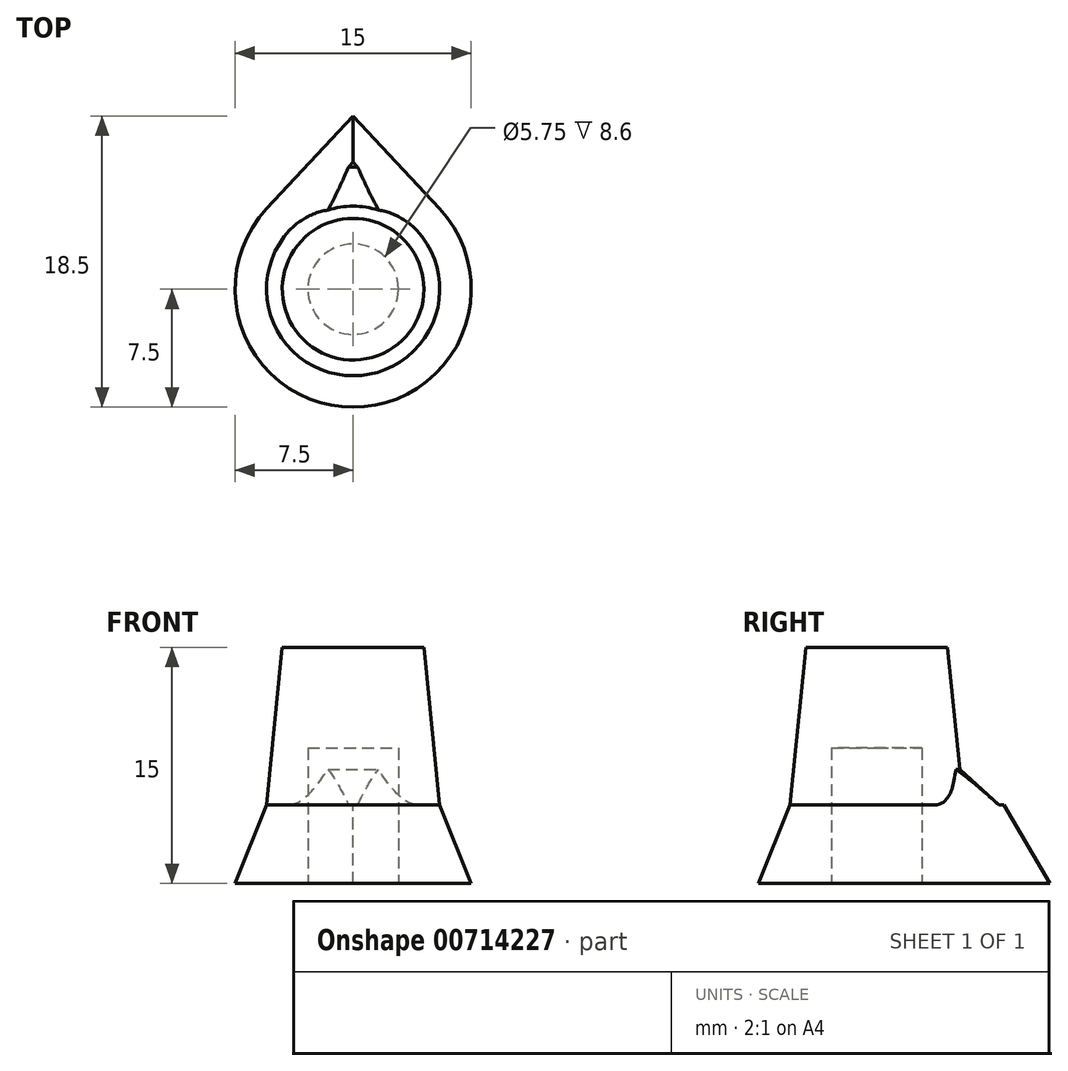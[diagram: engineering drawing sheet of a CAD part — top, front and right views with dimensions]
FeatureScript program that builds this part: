
annotation { "Feature Type Name" : "Feature", "Feature Type Description" : "" }
export const myFeature = defineFeature(function(context is Context, id is Id, definition is map)
    precondition{}
    {
        {
            var Q0;
            Q0=qCreatedBy(makeId("Top.planeOp"),FACE);
            var sketch = newSketch(context, id + "F0", { "sketchPlane" : qUnion([Q0])});
            skArc(sketch, "E0", {"start": v(-5.49, 5.11) * mm, "mid": v(0, -7.5) * mm, "end": v(5.49, 5.11) * mm});
            skLineSegment(sketch, "E1", {"start": v(-5.49, 5.11) * mm, "end": v(0, 11) * mm});
            skLineSegment(sketch, "E2", {"start": v(0, 11) * mm, "end": v(0, 0) * mm, "construction": true});
            skLineSegment(sketch, "E3.MirrorCS", {"start": v(5.49, 5.11) * mm, "end": v(0, 11) * mm});
            skSolve(sketch);
        }
        {
            var Q0;
            Q0=qCreatedBy(makeId("Top.planeOp"),FACE);
            cPlane(context, id + "F1", {"entities" : qUnion([Q0]), "cplaneType" : CPlaneType.OFFSET, "offset" : 5 * mm, "width" : 150 * mm, "height" : 150 * mm});
        }
        {
            var Q0;
            Q0=qCreatedBy(id+"F1.planeOp",FACE);
            var sketch = newSketch(context, id + "F2", { "sketchPlane" : qUnion([Q0])});
            skLineSegment(sketch, "E4.0", {"start": v(-4.02, 3.75) * mm, "end": v(0, 8.07) * mm});
            skArc(sketch, "E4.1", {"start": v(-4.02, 3.75) * mm, "mid": v(0, -5.5) * mm, "end": v(4.02, 3.75) * mm});
            skLineSegment(sketch, "E4.2", {"start": v(4.02, 3.75) * mm, "end": v(0, 8.07) * mm});
            skSolve(sketch);
        }
        {
            var Q0;
            Q0=makeQuery(id+"F0.imprint","IMPRINT",FACE,{"disambiguationData":[TD([[makeQuery(id+"F0.imprint","IMPRINT",EDGE,{"derivedFrom":sQuery(id+"F0.wireOp",EDGE,"E0")}),1.0]])]});
            var Q1;
            Q1=makeQuery(id+"F2.imprint","IMPRINT",FACE,{"disambiguationData":[TD([[makeQuery(id+"F2.imprint","IMPRINT",EDGE,{"derivedFrom":sQuery(id+"F2.wireOp",EDGE,"E4.0")}),-1.0]])]});
            loft(context, id + "F3", {"sheetProfilesArray" : [{ "sheetProfileEntities" : qUnion([Q0]) }, { "sheetProfileEntities" : qUnion([Q1]) }]});
        }
        {
            var Q0;
            Q0=makeQuery(id+"F3.opLoft","CAP_FACE",FACE,{"disambiguationData":[OSD([makeQuery(id+"F2.imprint","IMPRINT",FACE,{"disambiguationData":[TD([[makeQuery(id+"F2.imprint","IMPRINT",EDGE,{"derivedFrom":sQuery(id+"F2.wireOp",EDGE,"E4.0")}),-1.0]])]})])],"isStart":true});
            var sketch = newSketch(context, id + "F4", { "sketchPlane" : qUnion([Q0])});
            skArc(sketch, "E5.0", {"start": v(-4.02, 3.75) * mm, "mid": v(0, -5.5) * mm, "end": v(4.02, 3.75) * mm, "construction": true});
            skCircle(sketch, "E6", {"center": v(0, 0) * mm, "radius": 5.5 * mm});
            skSolve(sketch);
        }
        {
            var Q0;
            Q0 = qSketchRegion(id + "F4", true);
            var Q1;
            Q1 = qConstructionFilter(qBodyType(qCreatedBy(id + "F4" ,EDGE), BodyType.WIRE), ConstructionObject.NO);
            extrude(context, id + "F5", {"entities" : qUnion([Q0]), "operationType" : NewBodyOperationType.ADD, "surfaceOperationType" : NewSurfaceOperationType.ADD, "surfaceEntities" : qUnion([Q1]), "depth" : 10 * mm, "offsetDistance" : 25 * mm});
        }
        {
            var Q0;
            Q0=makeQuery(id+"F5.opExtrude","CAP_EDGE",EDGE,{"disambiguationData":[OSD([sQuery(id+"F4.wireOp",EDGE,"E6")])],"isStart":false});
            chamfer(context, id + "F6", {"entities" : qUnion([Q0]), "chamferType" : ChamferType.TWO_OFFSETS, "width1" : 1 * mm, "oppositeDirection" : false, "width2" : 10 * mm, "tangentPropagation" : true});
        }
        {
            var Q0;
            Q0=makeQuery(id+"F6.opChamfer","BLEND_EDGE",EDGE,{"blendedFrom":[makeQuery(id+"F5.opExtrude","CAP_EDGE",EDGE,{"disambiguationData":[OSD([sQuery(id+"F4.wireOp",EDGE,"E6")])],"isStart":false}),makeQuery(id+"F3.opLoft","CAP_FACE",FACE,{"disambiguationData":[OSD([makeQuery(id+"F2.imprint","IMPRINT",FACE,{"disambiguationData":[TD([[makeQuery(id+"F2.imprint","IMPRINT",EDGE,{"derivedFrom":sQuery(id+"F2.wireOp",EDGE,"E4.0")}),-1.0]])]})])],"isStart":true})],"blendedInto":[makeQuery(id+"F3.opLoft","CAP_FACE",FACE,{"disambiguationData":[OSD([makeQuery(id+"F2.imprint","IMPRINT",FACE,{"disambiguationData":[TD([[makeQuery(id+"F2.imprint","IMPRINT",EDGE,{"derivedFrom":sQuery(id+"F2.wireOp",EDGE,"E4.0")}),-1.0]])]})])],"isStart":true})]});
            chamfer(context, id + "F7", {"entities" : qUnion([Q0]), "width" : 2.5 * mm, "tangentPropagation" : true});
        }
        {
            var Q0;
            Q0=makeQuery(id+"F3.opLoft","CAP_FACE",FACE,{"disambiguationData":[OSD([makeQuery(id+"F0.imprint","IMPRINT",FACE,{"disambiguationData":[TD([[makeQuery(id+"F0.imprint","IMPRINT",EDGE,{"derivedFrom":sQuery(id+"F0.wireOp",EDGE,"E0")}),1.0]])]})])],"isStart":true});
            var sketch = newSketch(context, id + "F8", { "sketchPlane" : qUnion([Q0])});
            skCircle(sketch, "E7", {"center": v(0, 0) * mm, "radius": 2.88 * mm});
            skSolve(sketch);
        }
        {
            var Q0;
            Q0 = qSketchRegion(id + "F8", true);
            extrude(context, id + "F9", {"entities" : qUnion([Q0]), "operationType" : NewBodyOperationType.REMOVE, "oppositeDirection" : true, "depth" : 8.6 * mm, "offsetDistance" : 25 * mm});
        }
    });
